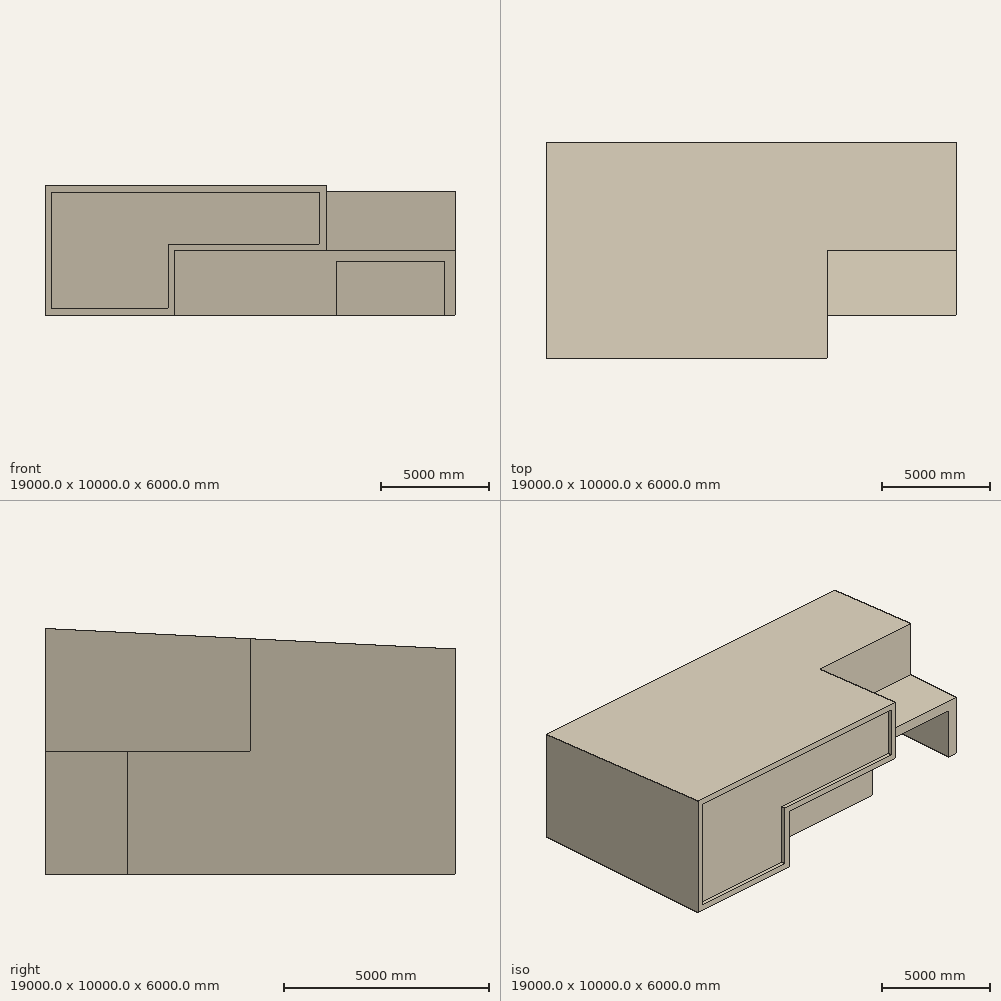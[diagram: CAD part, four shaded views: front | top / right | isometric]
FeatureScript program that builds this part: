
annotation { "Feature Type Name" : "Feature", "Feature Type Description" : "" }
export const myFeature = defineFeature(function(context is Context, id is Id, definition is map)
    precondition{}
    {
        {
            var Q0;
            Q0=qCreatedBy(makeId("Top.planeOp"),FACE);
            var sketch = newSketch(context, id + "F0", { "sketchPlane" : qUnion([Q0])});
            skLineSegment(sketch, "E0.bottom", {"start": v(3000, -5000) * mm, "end": v(-3000, -5000) * mm});
            skLineSegment(sketch, "E0.top", {"start": v(3000, 5000) * mm, "end": v(-3000, 5000) * mm});
            skLineSegment(sketch, "E0.left", {"start": v(3000, -5000) * mm, "end": v(3000, 5000) * mm});
            skLineSegment(sketch, "E0.right", {"start": v(-3000, -5000) * mm, "end": v(-3000, 5000) * mm});
            skPoint(sketch, "E0.middle", {"position": v(0, 0) * mm});
            skLineSegment(sketch, "E1.bottom", {"start": v(3000, 5000) * mm, "end": v(16000, 5000) * mm});
            skLineSegment(sketch, "E1.top", {"start": v(3000, -3000) * mm, "end": v(16000, -3000) * mm});
            skLineSegment(sketch, "E1.left", {"start": v(3000, 5000) * mm, "end": v(3000, -3000) * mm});
            skLineSegment(sketch, "E1.right", {"start": v(16000, 5000) * mm, "end": v(16000, -3000) * mm});
            skSolve(sketch);
        }
        {
            var Q0;
            Q0=makeQuery(id+"F0.imprint","IMPRINT",FACE,{"disambiguationData":[TD([[makeQuery(id+"F0.imprint","IMPRINT",EDGE,{"derivedFrom":sQuery(id+"F0.wireOp",EDGE,"E1.bottom")}),-1.0]])]});
            var Q1;
            Q1=makeQuery(id+"F0.imprint","IMPRINT",FACE,{"disambiguationData":[TD([[makeQuery(id+"F0.imprint","IMPRINT",EDGE,{"derivedFrom":sQuery(id+"F0.wireOp",EDGE,"E0.bottom")}),-1.0]])]});
            extrude(context, id + "F1", {"entities" : qUnion([Q0, Q1]), "depth" : 3000 * mm, "offsetDistance" : 25 * mm});
        }
        {
            var Q0;
            Q0=makeQuery(id+"F1.opExtrude","CAP_FACE",FACE,{"disambiguationData":[OSD([sQuery(id+"F0.wireOp",EDGE,"E0.bottom"),sQuery(id+"F0.wireOp",EDGE,"E0.top"),sQuery(id+"F0.wireOp",EDGE,"E0.left"),sQuery(id+"F0.wireOp",EDGE,"E0.right"),sQuery(id+"F0.wireOp",EDGE,"E1.bottom"),sQuery(id+"F0.wireOp",EDGE,"E1.top"),sQuery(id+"F0.wireOp",EDGE,"E1.right")])],"isStart":false});
            var sketch = newSketch(context, id + "F2", { "sketchPlane" : qUnion([Q0])});
            skLineSegment(sketch, "E2.bottom", {"start": v(-3000, 5000) * mm, "end": v(10000, 5000) * mm});
            skLineSegment(sketch, "E2.top", {"start": v(-3000, -5000) * mm, "end": v(10000, -5000) * mm});
            skLineSegment(sketch, "E2.left", {"start": v(-3000, 5000) * mm, "end": v(-3000, -5000) * mm});
            skLineSegment(sketch, "E2.right", {"start": v(10000, 5000) * mm, "end": v(10000, -5000) * mm});
            skPoint(sketch, "E3.oppositeSnap0", {"position": v(16000, 1000) * mm});
            skLineSegment(sketch, "E3.bottom", {"start": v(10000, 5000) * mm, "end": v(16000, 5000) * mm});
            skLineSegment(sketch, "E3.top", {"start": v(10000, 0) * mm, "end": v(16000, 0) * mm});
            skLineSegment(sketch, "E3.left", {"start": v(10000, 5000) * mm, "end": v(10000, 0) * mm});
            skLineSegment(sketch, "E3.right", {"start": v(16000, 5000) * mm, "end": v(16000, 0) * mm});
            skSolve(sketch);
        }
        {
            var Q0;
            {var subQ1=makeQuery(id+"F1.opExtrude","CAP_EDGE",EDGE,{"disambiguationData":[OSD([sQuery(id+"F0.wireOp",EDGE,"E0.left")])],"isStart":false});Q0=makeQuery(id+"F2.imprint","IMPRINT",FACE,{"disambiguationData":[TD([[makeQuery(id+"F2.imprint","IMPRINT",EDGE,{"derivedFrom":subQ1}),-1.0]])]});}
            var Q1;
            Q1=makeQuery(id+"F2.imprint","IMPRINT",FACE,{"disambiguationData":[TD([[makeQuery(id+"F2.imprint","IMPRINT",EDGE,{"derivedFrom":sQuery(id+"F2.wireOp",EDGE,"E2.bottom")}),-1.0]])]});
            var Q2;
            Q2=makeQuery(id+"F2.imprint","IMPRINT",FACE,{"disambiguationData":[TD([[makeQuery(id+"F2.imprint","IMPRINT",EDGE,{"derivedFrom":sQuery(id+"F2.wireOp",EDGE,"E3.bottom")}),-1.0]])]});
            extrude(context, id + "F3", {"entities" : qUnion([Q0, Q1, Q2]), "operationType" : NewBodyOperationType.ADD, "depth" : 3000 * mm, "offsetDistance" : 25 * mm});
        }
        {
            var Q0;
            Q0=makeQuery(id+"F1.opExtrude","SWEPT_FACE",FACE,{"disambiguationData":[OSD([sQuery(id+"F0.wireOp",EDGE,"E1.top")])]});
            var sketch = newSketch(context, id + "F4", { "sketchPlane" : qUnion([Q0])});
            skLineSegment(sketch, "E4.bottom", {"start": v(15500, 2500) * mm, "end": v(10500, 2500) * mm});
            skLineSegment(sketch, "E4.top", {"start": v(15500, 0) * mm, "end": v(10500, 0) * mm});
            skLineSegment(sketch, "E4.left", {"start": v(15500, 2500) * mm, "end": v(15500, 0) * mm});
            skLineSegment(sketch, "E4.right", {"start": v(10500, 2500) * mm, "end": v(10500, 0) * mm});
            skSolve(sketch);
        }
        {
            var Q0;
            Q0=makeQuery(id+"F4.imprint","IMPRINT",FACE,{"disambiguationData":[TD([[makeQuery(id+"F4.imprint","IMPRINT",EDGE,{"derivedFrom":sQuery(id+"F4.wireOp",EDGE,"E4.bottom")}),1.0]])]});
            extrude(context, id + "F5", {"entities" : qUnion([Q0]), "operationType" : NewBodyOperationType.REMOVE, "oppositeDirection" : true, "depth" : 7500 * mm, "offsetDistance" : 25 * mm});
        }
        {
            var Q0;
            Q0=makeQuery(id+"F3.boolean.opBoolean","MERGE",FACE,{"derivedFrom":[makeQuery(id+"F1.opExtrude","SWEPT_FACE",FACE,{"disambiguationData":[OSD([sQuery(id+"F0.wireOp",EDGE,"E0.right")])]}),makeQuery(id+"F3.opExtrude","SWEPT_FACE",FACE,{"disambiguationData":[OSD([sQuery(id+"F2.wireOp",EDGE,"E2.left")])]})]});
            var sketch = newSketch(context, id + "F6", { "sketchPlane" : qUnion([Q0])});
            skLineSegment(sketch, "E5", {"start": v(-5000, 5500) * mm, "end": v(5000, 6000) * mm});
            skLineSegment(sketch, "E6", {"start": v(5000, 6000) * mm, "end": v(-2735.78, 6000) * mm});
            skLineSegment(sketch, "E7", {"start": v(-2735.78, 6000) * mm, "end": v(-5000, 6000) * mm});
            skLineSegment(sketch, "E8", {"start": v(-5000, 6000) * mm, "end": v(-5000, 5500) * mm});
            skSolve(sketch);
        }
        {
            var Q0;
            Q0=makeQuery(id+"F6.imprint","IMPRINT",FACE,{"disambiguationData":[TD([[makeQuery(id+"F6.imprint","IMPRINT",EDGE,{"derivedFrom":sQuery(id+"F6.wireOp",EDGE,"E5")}),1.0]])]});
            extrude(context, id + "F7", {"entities" : qUnion([Q0]), "operationType" : NewBodyOperationType.REMOVE, "oppositeDirection" : true, "depth" : 22234.2 * mm, "offsetDistance" : 25 * mm});
        }
        {
            var Q0;
            Q0=makeQuery(id+"F3.boolean.opBoolean","MERGE",FACE,{"derivedFrom":[makeQuery(id+"F1.opExtrude","SWEPT_FACE",FACE,{"disambiguationData":[OSD([sQuery(id+"F0.wireOp",EDGE,"E0.bottom")])]}),makeQuery(id+"F3.opExtrude","SWEPT_FACE",FACE,{"disambiguationData":[OSD([sQuery(id+"F2.wireOp",EDGE,"E2.top")])]})]});
            var sketch = newSketch(context, id + "F8", { "sketchPlane" : qUnion([Q0])});
            skLineSegment(sketch, "E9.0", {"start": v(-3000, 6000) * mm, "end": v(10000, 6000) * mm});
            skLineSegment(sketch, "E10.0", {"start": v(-3000, 6000) * mm, "end": v(-3000, 0) * mm});
            skLineSegment(sketch, "E11.0", {"start": v(10000, 6000) * mm, "end": v(10000, 3000) * mm});
            skLineSegment(sketch, "E12.0", {"start": v(3000, 3000) * mm, "end": v(10000, 3000) * mm});
            skLineSegment(sketch, "E13.0", {"start": v(3000, 3000) * mm, "end": v(3000, 0) * mm});
            skLineSegment(sketch, "E14.0", {"start": v(3000, 0) * mm, "end": v(-3000, 0) * mm});
            skLineSegment(sketch, "E15.0", {"start": v(-2700, 5700) * mm, "end": v(9700, 5700) * mm});
            skLineSegment(sketch, "E15.1", {"start": v(2700, 300) * mm, "end": v(-2700, 300) * mm});
            skLineSegment(sketch, "E15.2", {"start": v(2700, 3300) * mm, "end": v(2700, 300) * mm});
            skLineSegment(sketch, "E15.3", {"start": v(-2700, 5700) * mm, "end": v(-2700, 300) * mm});
            skLineSegment(sketch, "E15.4", {"start": v(2700, 3300) * mm, "end": v(9700, 3300) * mm});
            skLineSegment(sketch, "E15.5", {"start": v(9700, 5700) * mm, "end": v(9700, 3300) * mm});
            skSolve(sketch);
        }
        {
            var Q0;
            Q0=makeQuery(id+"F8.imprint","IMPRINT",FACE,{"disambiguationData":[TD([[makeQuery(id+"F8.imprint","IMPRINT",EDGE,{"derivedFrom":sQuery(id+"F8.wireOp",EDGE,"E15.0")}),-1.0]])]});
            extrude(context, id + "F9", {"entities" : qUnion([Q0]), "operationType" : NewBodyOperationType.REMOVE, "oppositeDirection" : true, "depth" : 200 * mm, "offsetDistance" : 25 * mm});
        }
    });
